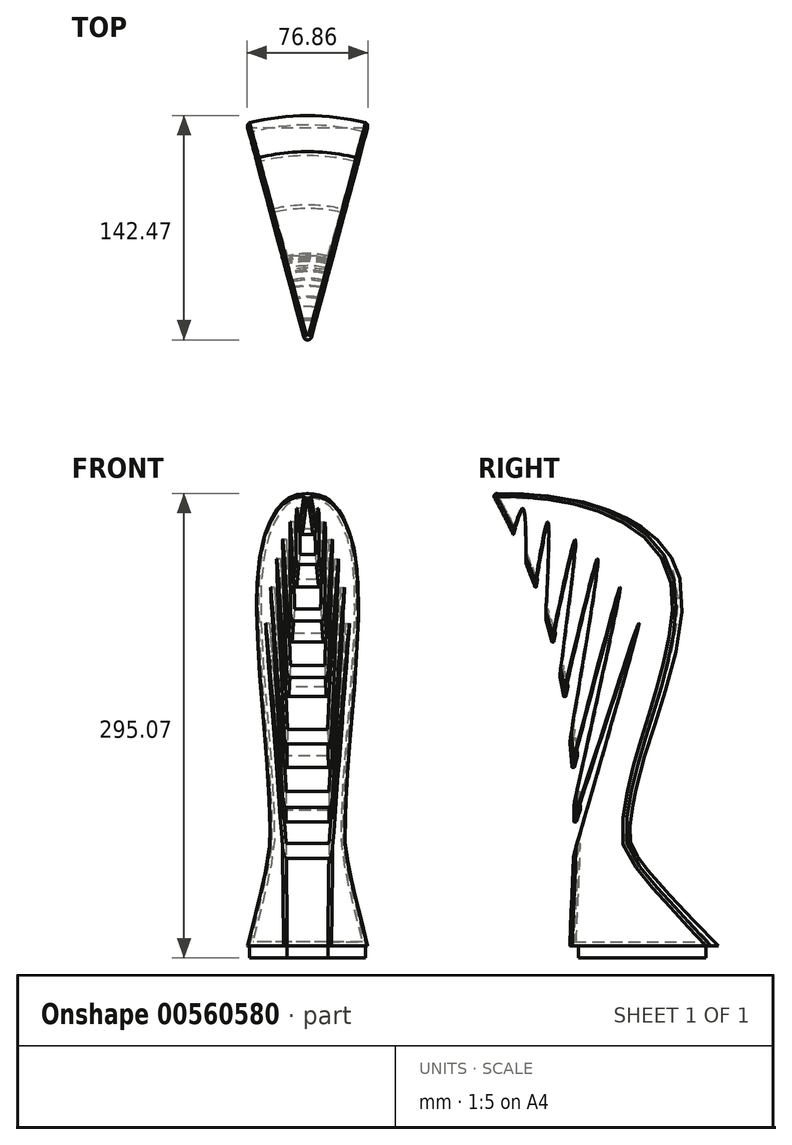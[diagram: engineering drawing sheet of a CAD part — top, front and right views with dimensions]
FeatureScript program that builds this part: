
annotation { "Feature Type Name" : "Feature", "Feature Type Description" : "" }
export const myFeature = defineFeature(function(context is Context, id is Id, definition is map)
    precondition{}
    {
        {
            var Q0;
            Q0=qCreatedBy(makeId("Right.planeOp"),FACE);
            var sketch = newSketch(context, id + "F0", { "sketchPlane" : qUnion([Q0])});
            skFitSpline(sketch, "E0", {"points": [v(-78.47, 129.02) * mm, v(0, 116.6) * mm, v(41.47, 72.29) * mm, v(17.56, -41.86) * mm, v(9.7, -79.98) * mm, v(10.09, -93.74) * mm, v(65.45, -158.56) * mm], "startDerivative": vector(538, 0) * mm, "endDerivative": vector(487.03, -505.44) * mm});
            skFitSpline(sketch, "E1", {"points": [v(-78.47, 129.02) * mm, v(-27.15, -158.56) * mm], "startDerivative": vector(215.35, -370.03) * mm, "endDerivative": vector(1.62, -143.05) * mm});
            skLineSegment(sketch, "E2", {"start": v(-27.15, -158.56) * mm, "end": v(65.45, -158.56) * mm});
            skFitSpline(sketch, "E3", {"points": [v(-64.61, 103.01) * mm, v(-57.93, 119.42) * mm, v(-55.9, 83.71) * mm], "startDerivative": vector(18.96, 60.46) * mm, "endDerivative": vector(-0.3, -90.29) * mm});
            skFitSpline(sketch, "E4", {"points": [v(-50.24, 69.44) * mm, v(-41.56, 110.97) * mm, v(-43, 48.12) * mm], "startDerivative": vector(24.65, 138.76) * mm, "endDerivative": vector(-9.05, -171.26) * mm});
            skFitSpline(sketch, "E5", {"points": [v(-39.12, 34.64) * mm, v(-23.5, 99.7) * mm, v(-33.77, 12.12) * mm], "startDerivative": vector(45.88, 210.14) * mm, "endDerivative": vector(-33.44, -244.73) * mm});
            skFitSpline(sketch, "E6", {"points": [v(-31.45, 0) * mm, v(-8.7, 87.46) * mm, v(-27.26, -30.07) * mm], "startDerivative": vector(68.16, 282.6) * mm, "endDerivative": vector(-57.19, -328.75) * mm});
            skFitSpline(sketch, "E7", {"points": [v(-25.96, -45) * mm, v(6.06, 69.33) * mm, v(-24.8, -70.59) * mm], "startDerivative": vector(96.92, 360.29) * mm, "endDerivative": vector(-91.86, -399.53) * mm});
            skFitSpline(sketch, "E8", {"points": [v(-24.7, -79.65) * mm, v(18.37, 46.47) * mm, v(-25.01, -102.68) * mm], "startDerivative": vector(131.75, 394.28) * mm, "endDerivative": vector(-128.5, -429.87) * mm});
            skFitSpline(sketch, "E9.trimOffspring", {"points": [v(-78.47, 129.02) * mm, v(-27.15, -158.56) * mm], "startDerivative": vector(215.35, -370.03) * mm, "endDerivative": vector(1.62, -143.05) * mm});
            skFitSpline(sketch, "E10.trimOffspring", {"points": [v(-78.47, 129.02) * mm, v(-27.15, -158.56) * mm], "startDerivative": vector(215.35, -370.03) * mm, "endDerivative": vector(1.62, -143.05) * mm});
            skFitSpline(sketch, "E11.trimOffspring", {"points": [v(-78.47, 129.02) * mm, v(-27.15, -158.56) * mm], "startDerivative": vector(215.35, -370.03) * mm, "endDerivative": vector(1.62, -143.05) * mm});
            skFitSpline(sketch, "E12.trimOffspring", {"points": [v(-78.47, 129.02) * mm, v(-27.15, -158.56) * mm], "startDerivative": vector(215.35, -370.03) * mm, "endDerivative": vector(1.62, -143.05) * mm});
            skLineSegment(sketch, "E13", {"start": v(-84.35, 129.02) * mm, "end": v(-84.35, 14.68) * mm});
            skSolve(sketch);
        }
        {
            var Q0;
            Q0=makeQuery(id+"F0.imprint","IMPRINT",FACE,{"disambiguationData":[TD([[makeQuery(id+"F0.imprint","IMPRINT",EDGE,{"derivedFrom":sQuery(id+"F0.wireOp",EDGE,"E0")}),-1.0]])]});
            var Q1;
            Q1=sQuery(id+"F0.wireOp",EDGE,"E13");
            revolve(context, id + "F1", {"entities" : qUnion([Q0]), "axis" : qUnion([Q1]), "revolveType" : RevolveType.SYMMETRIC, "angle" : 30 * degree});
        }
        {
            var Q0;
            Q0=makeQuery(id+"F1.opRevolve","SWEPT_FACE",FACE,{"disambiguationData":[OSD([sQuery(id+"F0.wireOp",EDGE,"E3")])]});
            var Q1;
            Q1=makeQuery(id+"F1.opRevolve","SWEPT_FACE",FACE,{"disambiguationData":[OSD([sQuery(id+"F0.wireOp",EDGE,"E4")])]});
            var Q2;
            Q2=makeQuery(id+"F1.opRevolve","SWEPT_FACE",FACE,{"disambiguationData":[OSD([sQuery(id+"F0.wireOp",EDGE,"E5")])]});
            var Q3;
            Q3=makeQuery(id+"F1.opRevolve","SWEPT_FACE",FACE,{"disambiguationData":[OSD([sQuery(id+"F0.wireOp",EDGE,"E6")])]});
            var Q4;
            Q4=makeQuery(id+"F1.opRevolve","SWEPT_FACE",FACE,{"disambiguationData":[OSD([sQuery(id+"F0.wireOp",EDGE,"E7")])]});
            var Q5;
            Q5=makeQuery(id+"F1.opRevolve","SWEPT_FACE",FACE,{"disambiguationData":[OSD([sQuery(id+"F0.wireOp",EDGE,"E8")])]});
            shell(context, id + "F2", {"entities" : qUnion([Q0, Q1, Q2, Q3, Q4, Q5]), "thickness" : 2.54 * mm});
        }
        {
            var Q0;
            Q0=makeQuery(id+"F1.opRevolve","CAP_EDGE",EDGE,{"disambiguationData":[OSD([sQuery(id+"F0.wireOp",EDGE,"E1")])],"isStart":false});
            var Q1;
            Q1=makeQuery(id+"F1.opRevolve","CAP_EDGE",EDGE,{"disambiguationData":[OSD([sQuery(id+"F0.wireOp",EDGE,"E1")])],"isStart":true});
            var Q2;
            Q2=makeQuery(id+"F1.opRevolve","CAP_EDGE",EDGE,{"disambiguationData":[OSD([sQuery(id+"F0.wireOp",EDGE,"E9.trimOffspring")])],"isStart":false});
            var Q3;
            Q3=makeQuery(id+"F1.opRevolve","CAP_EDGE",EDGE,{"disambiguationData":[OSD([sQuery(id+"F0.wireOp",EDGE,"E9.trimOffspring")])],"isStart":true});
            var Q4;
            Q4=makeQuery(id+"F1.opRevolve","CAP_EDGE",EDGE,{"disambiguationData":[OSD([sQuery(id+"F0.wireOp",EDGE,"E10.trimOffspring")])],"isStart":false});
            var Q5;
            Q5=makeQuery(id+"F1.opRevolve","CAP_EDGE",EDGE,{"disambiguationData":[OSD([sQuery(id+"F0.wireOp",EDGE,"E10.trimOffspring")])],"isStart":true});
            var Q6;
            Q6=makeQuery(id+"F1.opRevolve","CAP_EDGE",EDGE,{"disambiguationData":[OSD([sQuery(id+"F0.wireOp",EDGE,"E11.trimOffspring")])],"isStart":false});
            var Q7;
            Q7=makeQuery(id+"F1.opRevolve","CAP_EDGE",EDGE,{"disambiguationData":[OSD([sQuery(id+"F0.wireOp",EDGE,"E11.trimOffspring")])],"isStart":true});
            var Q8;
            Q8=makeQuery(id+"F1.opRevolve","CAP_EDGE",EDGE,{"disambiguationData":[OSD([sQuery(id+"F0.wireOp",EDGE,"E12.trimOffspring")])],"isStart":false});
            var Q9;
            Q9=makeQuery(id+"F1.opRevolve","CAP_EDGE",EDGE,{"disambiguationData":[OSD([sQuery(id+"F0.wireOp",EDGE,"E12.trimOffspring")])],"isStart":true});
            var Q10;
            Q10=makeQuery(id+"F1.opRevolve","CAP_EDGE",EDGE,{"disambiguationData":[OSD([sQuery(id+"F0.wireOp",EDGE,"E12.trimOffspring")])],"isStart":false});
            var Q11;
            Q11=makeQuery(id+"F1.opRevolve","CAP_EDGE",EDGE,{"disambiguationData":[OSD([sQuery(id+"F0.wireOp",EDGE,"E12.trimOffspring")])],"isStart":true});
            var Q12;
            Q12=makeQuery(id+"F1.opRevolve","CAP_EDGE",EDGE,{"disambiguationData":[OSD([sQuery(id+"F0.wireOp",EDGE,"E10.trimOffspring")])],"isStart":false});
            var Q13;
            Q13=makeQuery(id+"F1.opRevolve","SWEPT_EDGE",EDGE,{"disambiguationData":[OSD([sQuery(id+"F0.wireOp",EDGE,"E0"),sQuery(id+"F0.wireOp",EDGE,"E1")])]});
            var Q14;
            Q14=makeQuery(id+"F1.opRevolve","CAP_EDGE",EDGE,{"disambiguationData":[OSD([sQuery(id+"F0.wireOp",EDGE,"E0")])],"isStart":false});
            var Q15;
            Q15=makeQuery(id+"F1.opRevolve","CAP_EDGE",EDGE,{"disambiguationData":[OSD([sQuery(id+"F0.wireOp",EDGE,"E0")])],"isStart":true});
            var Q16;
            Q16=makeQuery(id+"F1.opRevolve","CAP_EDGE",EDGE,{"disambiguationData":[OSD([sQuery(id+"F0.wireOp",EDGE,"E10.trimOffspring")])],"isStart":true});
            fillet(context, id + "F3", {"entities" : qUnion([Q0, Q1, Q2, Q3, Q4, Q5, Q6, Q7, Q8, Q9, Q10, Q11, Q12, Q13, Q14, Q15, Q16]), "radius" : 2 * mm, "tangentPropagation" : true, "allowEdgeOverflow" : false});
        }
        {
            var Q0;
            Q0=makeQuery(id+"F1.opRevolve","SWEPT_FACE",FACE,{"disambiguationData":[OSD([sQuery(id+"F0.wireOp",EDGE,"E2")])]});
            var sketch = newSketch(context, id + "F4", { "sketchPlane" : qUnion([Q0])});
            skLineSegment(sketch, "E14", {"start": v(-12.93, 23.56) * mm, "end": v(12.93, 23.56) * mm});
            skLineSegment(sketch, "E15", {"start": v(12.93, 23.56) * mm, "end": v(36.82, -57.65) * mm});
            skLineSegment(sketch, "E16", {"start": v(36.82, -57.65) * mm, "end": v(-36.82, -57.65) * mm});
            skLineSegment(sketch, "E17", {"start": v(-36.82, -57.65) * mm, "end": v(-12.93, 23.56) * mm});
            skSolve(sketch);
        }
        {
            var Q0;
            Q0=makeQuery(id+"F4.imprint","IMPRINT",FACE,{"disambiguationData":[TD([[makeQuery(id+"F4.imprint","IMPRINT",EDGE,{"derivedFrom":sQuery(id+"F4.wireOp",EDGE,"E14")}),-1.0]])]});
            extrude(context, id + "F5", {"entities" : qUnion([Q0]), "operationType" : NewBodyOperationType.ADD, "depth" : 7.5 * mm, "offsetDistance" : 25.4 * mm});
        }
    });
